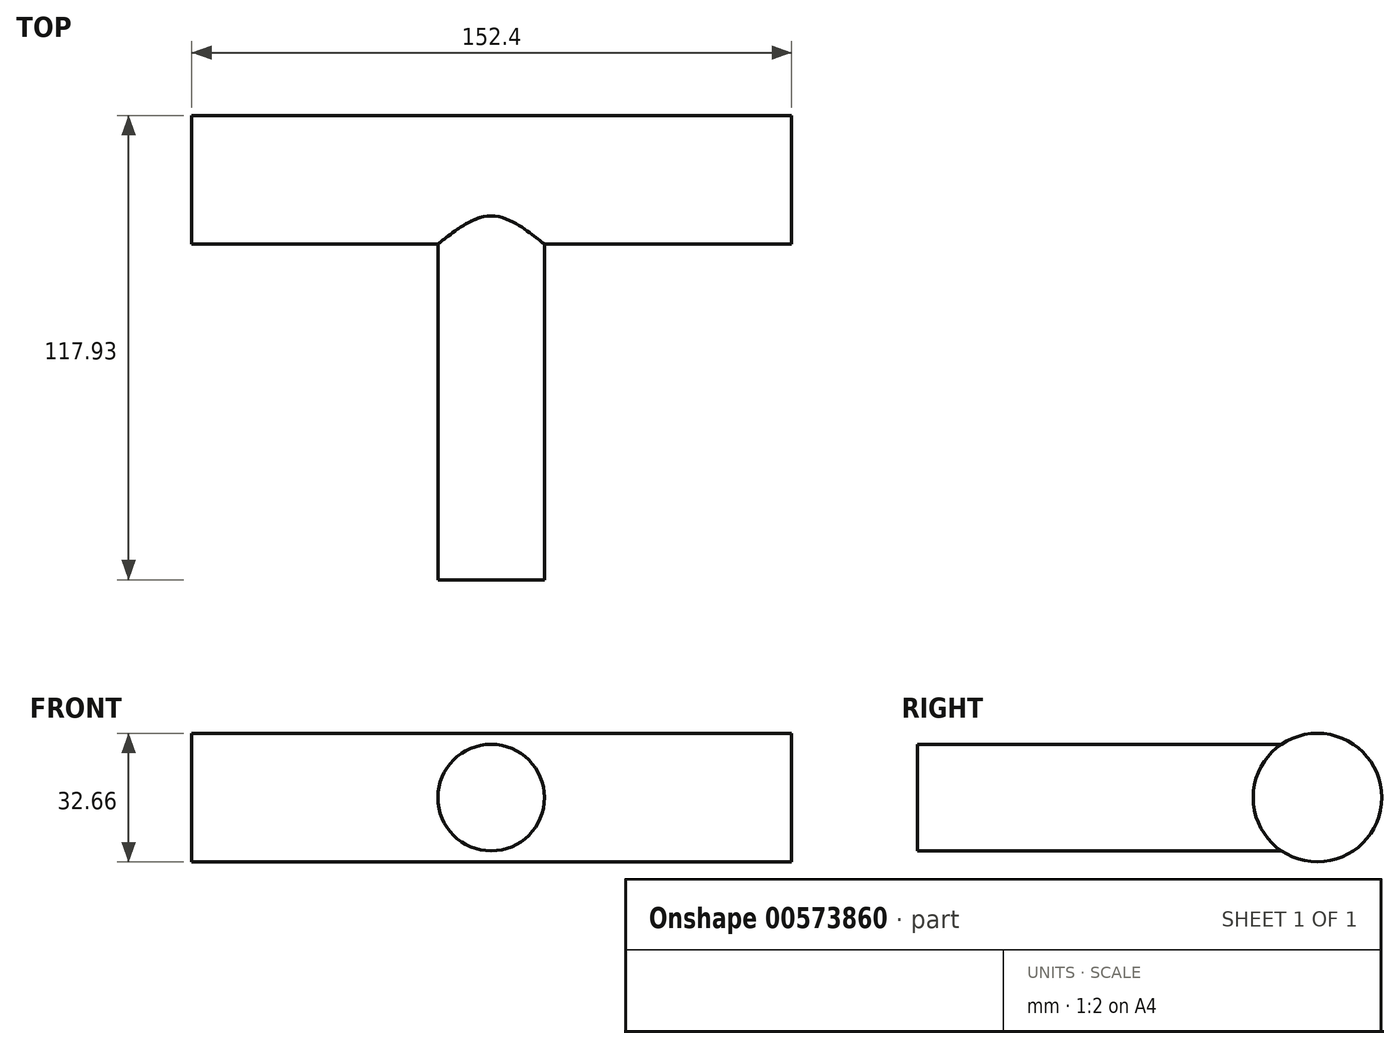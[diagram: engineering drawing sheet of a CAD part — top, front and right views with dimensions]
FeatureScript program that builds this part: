
annotation { "Feature Type Name" : "Feature", "Feature Type Description" : "" }
export const myFeature = defineFeature(function(context is Context, id is Id, definition is map)
    precondition{}
    {
        {
            var Q0;
            Q0=qCreatedBy(makeId("Right.planeOp"),FACE);
            var sketch = newSketch(context, id + "F0", { "sketchPlane" : qUnion([Q0])});
            skCircle(sketch, "E0", {"center": v(0, 0) * mm, "radius": 16.33 * mm});
            skSolve(sketch);
        }
        {
            var Q0;
            Q0 = qSketchRegion(id + "F0", true);
            extrude(context, id + "F1", {"entities" : qUnion([Q0]), "depth" : 152.4 * mm, "offsetDistance" : 25.4 * mm});
        }
        {
            var Q0;
            Q0=qCreatedBy(makeId("Front.planeOp"),FACE);
            var sketch = newSketch(context, id + "F2", { "sketchPlane" : qUnion([Q0])});
            skCircle(sketch, "E1", {"center": v(76.08, 0) * mm, "radius": 13.53 * mm});
            skSolve(sketch);
        }
        {
            var Q0;
            Q0 = qSketchRegion(id + "F2", true);
            extrude(context, id + "F3", {"entities" : qUnion([Q0]), "operationType" : NewBodyOperationType.ADD, "depth" : 101.6 * mm, "offsetDistance" : 25.4 * mm});
        }
    });
